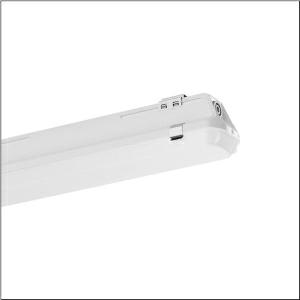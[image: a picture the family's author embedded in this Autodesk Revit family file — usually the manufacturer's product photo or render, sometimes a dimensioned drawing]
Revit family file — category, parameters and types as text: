
# Revit family: monsun_r__11_51fp12mp4b0q_eb41
name_source: partatom
category: Lighting Fixtures
units: mm (PartAtom-declared; Revit-internal decimal feet)

## family parameters
Cut with Voids When Loaded = No
Host = Face
Light Source = No
Part Type = Normal
Room Calculation Point = No
Round Connector Dimension = Use Diameter
Shared = No

## types (1)
- --- (1 x LED, 11850 lm, 66.2 W, 4000K)
    Apparent Load = 66 VA
    CIE Flux Codes = 62 86 96 97 100
    Color Rendering = 80
    Color Temperature = 4000K
    Default Elevation = 1800 mm
    Description = Monsun® 11, damp-proof luminaire, chain hanger, primary light control with lens, primary optical cover: enclosure, of PMMA, light emission: direct distribution, primary light characteristic: symmetric, installation type: suspended mounting, surface-mounted, horizontal mounting, vertical mounting, LED, rated luminous flux: 11.850lm, luminous efficacy: 179lm/W, light colour: 840, colour temperature: 4000K, control gear: ECG, with terminal, 3-pole, max. 2.5mm², mains connection: 220..240V, AC, 50/60Hz, rated input power: 66W, luminaire housing, of glass-fibre reinforced polyester, uncoated, bright grey, incl. chain hanger, length: 1.590mm, width: 90mm, height: 88mm, clip for enclosure, of stainless steel (V2A), ceiling mounting element, of stainless steel (V2A), chain hanger, of stainless steel (V2A), protection rating (complete): IP66, insulation class (complete): insulation class I (protective earthing), certification: CE, ENEC, VDE, UKCA, protection symbol: D, impact resistance: IK04, permissible operating ambient temperature: -35..+35°C, standard: EN 50419, EN 60598-2-1, no direct snow, no direct sun, no direct rain, for indoor or canopied outdoor use, corresponds to IFS (International Featured Standards) requirements for safety and quality in the food industry, contact your sales advisor before using the luminaires in applications with unclear chemical exposure, large temperature fluctuations or condensation-forming humidity, LABS conformity tested according to VDMA 24364:2018-05, packaging unit: 1 piece
    Height = 89 mm
    Lamp = 1 x LED
    Lamp Light Flux = 11850 lm
    Lamp Power = 66.2 W
    Lamp count = 1
    Length = 1590 mm
    Luminous efficacy = 179 lm/W
    Manufacturer = Siteco
    ModVariant = No
    Model = 51FP12MP4B0Q
    Mounting Place = Ceiling
    Mounting Type = Surface mounted
    Number of Poles = 1
    OnlyDefault = Yes
    Power Factor = 1
    Product Name = Monsun® 11
    Product group = damp-proof luminaire
    ProductGroupID = 300
    Protection Class = Protection class I
    Protection Degree = IP 66
    RLX_Detail_Level = 1
    RLX_Emergency_Light_Flux = 0 lm
    RLX_Emergency_Type = 0
    RLX_Emergency_Type_DB = No
    RlxData = <blob elided: 89985 chars, md5=be472161>
    Socket = socket
    Standby Power = 0 W
    System Light Flux = 11850 lm
    System Power = 66 W
    Type Comments = factory setting: luminous flux: 100 % | (A | C | E) | 155 mA
    Type Image = l_1319650.jpg
    URL = http://relux.com
    VarID = @adj_174641
    Voltage = 0 V
    Weight = 0.00 kg
    Width = 90 mm

## geometry (parser evidence)
native form markers: Blend x4, Sweep x11
no freeform markers — native parametric forms only
